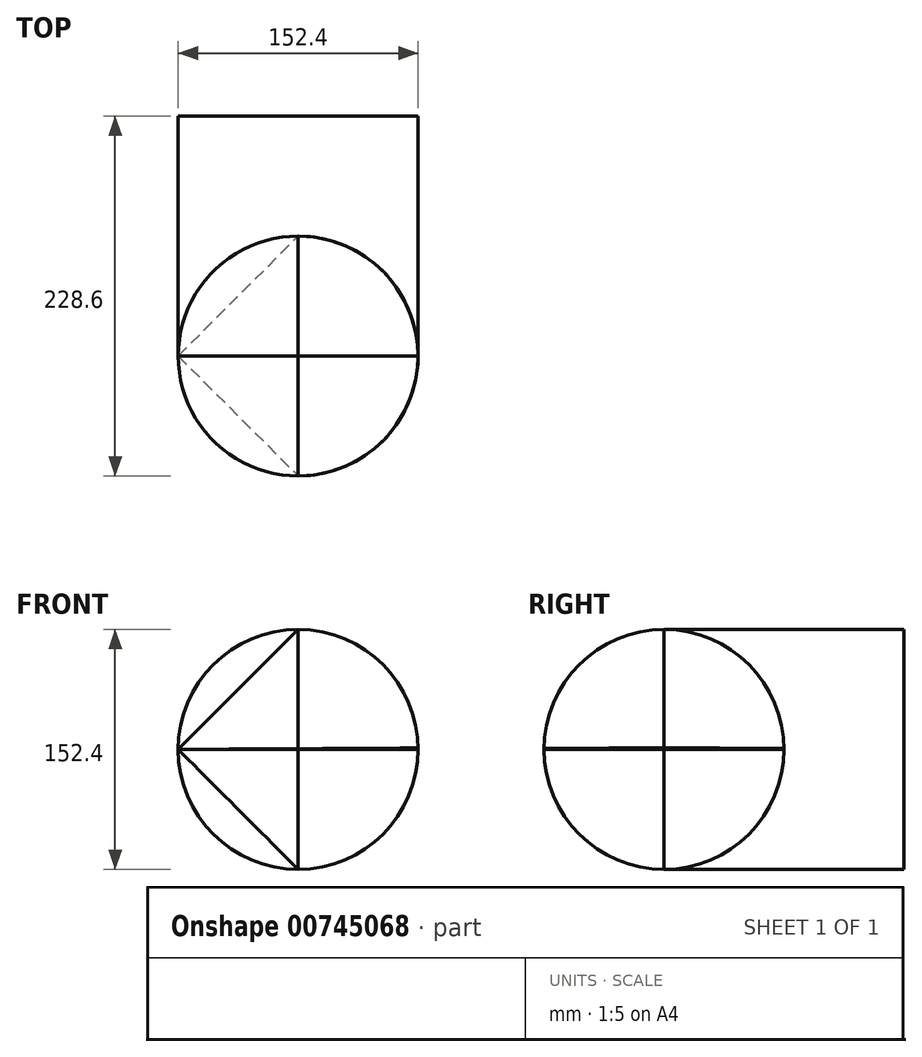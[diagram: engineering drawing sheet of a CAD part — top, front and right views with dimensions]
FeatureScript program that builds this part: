
annotation { "Feature Type Name" : "Feature", "Feature Type Description" : "" }
export const myFeature = defineFeature(function(context is Context, id is Id, definition is map)
    precondition{}
    {
        {
            var Q0;
            Q0=qCreatedBy(makeId("Top.planeOp"),FACE);
            var sketch = newSketch(context, id + "F0", { "sketchPlane" : qUnion([Q0])});
            skLineSegment(sketch, "E0", {"start": v(76.2, 0) * mm, "end": v(0, 0) * mm});
            skLineSegment(sketch, "E1", {"start": v(0, 0) * mm, "end": v(-76.2, 0) * mm});
            skArc(sketch, "E2", {"start": v(76.2, 0) * mm, "mid": v(0, 76.2) * mm, "end": v(-76.2, 0) * mm});
            skLineSegment(sketch, "E3", {"start": v(-76.2, 0) * mm, "end": v(-76.2, -78.48) * mm});
            skArc(sketch, "E4", {"start": v(-76.2, 0) * mm, "mid": v(0, -76.2) * mm, "end": v(76.2, 0) * mm});
            skSolve(sketch);
        }
        {
            var Q0;
            Q0=qCreatedBy(makeId("Front.planeOp"),FACE);
            var sketch = newSketch(context, id + "F1", { "sketchPlane" : qUnion([Q0])});
            skLineSegment(sketch, "E5", {"start": v(0, 0) * mm, "end": v(0, 76.2) * mm});
            skCircle(sketch, "E6", {"center": v(0, 0) * mm, "radius": 76.2 * mm});
            skSolve(sketch);
        }
        {
            var Q0;
            Q0=qCreatedBy(makeId("Front.planeOp"),FACE);
            var sketch = newSketch(context, id + "F2", { "sketchPlane" : qUnion([Q0])});
            skLineSegment(sketch, "E7", {"start": v(-76.2, 0) * mm, "end": v(0, 76.2) * mm});
            skLineSegment(sketch, "E8", {"start": v(-76.2, 0) * mm, "end": v(0, 0) * mm});
            skLineSegment(sketch, "E9", {"start": v(0, 0) * mm, "end": v(0, 76.2) * mm});
            skSolve(sketch);
        }
        {
            var Q0;
            Q0=makeQuery(id+"F2.imprint","IMPRINT",FACE,{"disambiguationData":[TD([[makeQuery(id+"F2.imprint","IMPRINT",EDGE,{"derivedFrom":sQuery(id+"F2.wireOp",EDGE,"E7")}),-1.0]])]});
            var Q1;
            Q1=sQuery(id+"F2.wireOp",EDGE,"E7");
            var Q2;
            Q2=sQuery(id+"F0.wireOp",EDGE,"E0");
            revolve(context, id + "F3", {"surfaceOperationType" : NewSurfaceOperationType.NEW, "entities" : qUnion([Q0]), "surfaceEntities" : qUnion([Q1]), "axis" : qUnion([Q2]), "revolveType" : RevolveType.ONE_DIRECTION, "angle" : 360 * degree});
        }
        {
            var Q0;
            Q0=makeQuery(id+"F0.imprint","IMPRINT",FACE,{"disambiguationData":[TD([[makeQuery(id+"F0.imprint","IMPRINT",EDGE,{"derivedFrom":sQuery(id+"F0.wireOp",EDGE,"E0")}),-1.0]])]});
            var Q1;
            Q1=makeQuery(id+"F0.imprint","IMPRINT",FACE,{"disambiguationData":[TD([[makeQuery(id+"F0.imprint","IMPRINT",EDGE,{"derivedFrom":sQuery(id+"F0.wireOp",EDGE,"E0")}),1.0]])]});
            var Q2;
            Q2=sQuery(id+"F0.wireOp",EDGE,"E2");
            var Q3;
            Q3=sQuery(id+"F0.wireOp",EDGE,"E3");
            revolve(context, id + "F4", {"surfaceOperationType" : NewSurfaceOperationType.NEW, "entities" : qUnion([Q0, Q1]), "surfaceEntities" : qUnion([Q2]), "axis" : qUnion([Q3]), "revolveType" : RevolveType.ONE_DIRECTION, "oppositeDirection" : true, "angle" : 359.66 * degree});
        }
        {
            var Q0;
            {var subQ0=sQuery(id+"F1.wireOp",EDGE,"E6");Q0=makeQuery(id+"F1.imprint","IMPRINT",FACE,{"disambiguationData":[TD([[makeQuery(id+"F1.imprint","IMPRINT",EDGE,{"disambiguationData":[TD([[makeQuery(id+"F1.imprint","IMPRINT",VERTEX,{"derivedFrom":subQ0}),-1.0]])],"derivedFrom":subQ0}),1.0]])]});}
            var Q1;
            Q1=sQuery(id+"F1.wireOp",EDGE,"E6");
            extrude(context, id + "F5", {"entities" : qUnion([Q0]), "surfaceEntities" : qUnion([Q1]), "oppositeDirection" : true, "depth" : 152.4 * mm, "offsetDistance" : 25.4 * mm});
        }
    });
